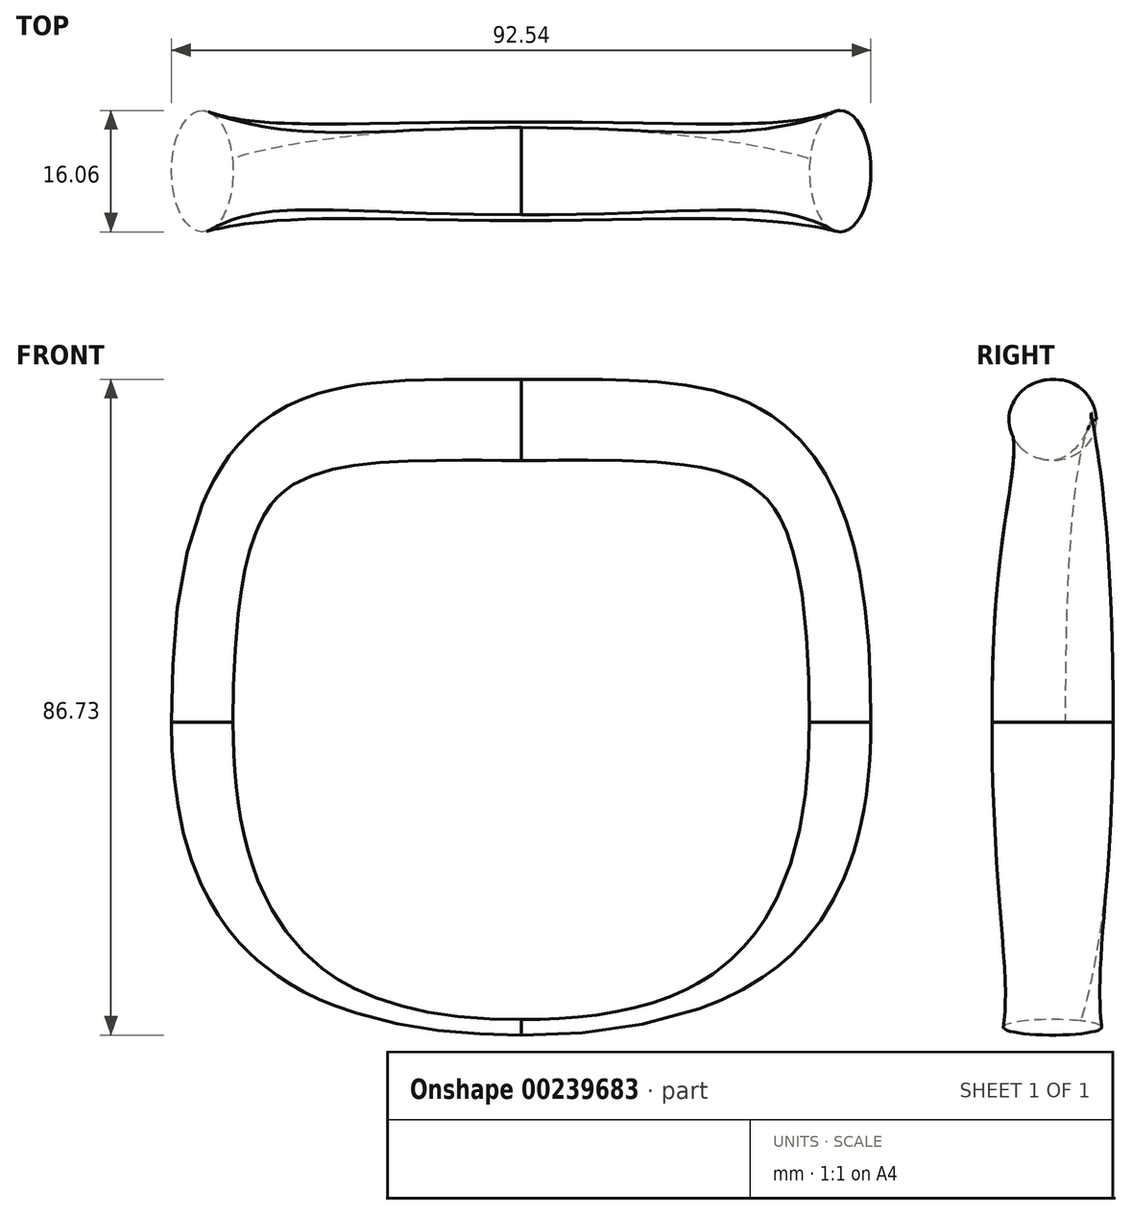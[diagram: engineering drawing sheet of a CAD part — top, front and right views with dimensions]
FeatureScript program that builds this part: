
annotation { "Feature Type Name" : "Feature", "Feature Type Description" : "" }
export const myFeature = defineFeature(function(context is Context, id is Id, definition is map)
    precondition{}
    {
        {
            var Q0;
            Q0=qCreatedBy(makeId("Right.planeOp"),FACE);
            var sketch = newSketch(context, id + "F0", { "sketchPlane" : qUnion([Q0])});
            skEllipse(sketch, "E0", {"center": v(0, 40) * mm, "majorRadius": 5.78 * mm, "minorRadius": 5.36 * mm, "majorAxis": v(1, 0)});
            skEllipse(sketch, "E1", {"center": v(0, -40.34) * mm, "majorRadius": 6.51 * mm, "minorRadius": 1.03 * mm, "majorAxis": v(1, 0)});
            skSolve(sketch);
        }
        {
            var Q0;
            Q0=qCreatedBy(makeId("Top.planeOp"),FACE);
            var sketch = newSketch(context, id + "F1", { "sketchPlane" : qUnion([Q0])});
            skEllipse(sketch, "E2", {"center": v(-42.2, 0) * mm, "majorRadius": 8.03 * mm, "minorRadius": 4.07 * mm, "majorAxis": v(0, 1)});
            skEllipse(sketch, "E3.MirrorC", {"center": v(42.2, 0) * mm, "majorRadius": 8.03 * mm, "minorRadius": 4.07 * mm, "majorAxis": v(0, 1)});
            skSolve(sketch);
        }
        {
            var Q0;
            Q0=qCreatedBy(makeId("Front.planeOp"),FACE);
            var sketch = newSketch(context, id + "F2", { "sketchPlane" : qUnion([Q0])});
            skFitSpline(sketch, "E4", {"points": [v(0, 40.05) * mm, v(42.43, 0) * mm, v(0, -40.58) * mm, v(-42.09, 0) * mm, v(0, 40.05) * mm]});
            skSolve(sketch);
        }
        {
            var Q0;
            Q0=qCreatedBy(makeId("Right.planeOp"),FACE);
            cPlane(context, id + "F3", {"entities" : qUnion([Q0]), "cplaneType" : CPlaneType.OFFSET, "offset" : 1 * mm, "oppositeDirection" : true, "width" : 150 * mm, "height" : 150 * mm});
        }
        {
            var Q0;
            Q0=makeQuery(id+"F0.imprint","IMPRINT",FACE,{"disambiguationData":[TD([[makeQuery(id+"F0.imprint","IMPRINT",EDGE,{"derivedFrom":sQuery(id+"F0.wireOp",EDGE,"E0")}),1.0]])]});
            var Q1;
            Q1=makeQuery(id+"F1.imprint","IMPRINT",FACE,{"disambiguationData":[TD([[makeQuery(id+"F1.imprint","IMPRINT",EDGE,{"derivedFrom":sQuery(id+"F1.wireOp",EDGE,"E3.MirrorC")}),1.0]])]});
            var Q2;
            Q2=sQuery(id+"F2.wireOp",EDGE,"E4");
            loft(context, id + "F4", {"startCondition" : LoftEndDerivativeType.NORMAL_TO_PROFILE, "startMagnitude" : 2, "endCondition" : LoftEndDerivativeType.NORMAL_TO_PROFILE, "endMagnitude" : 3, "sheetProfilesArray" : [{ "sheetProfileEntities" : qUnion([Q0]) }, { "sheetProfileEntities" : qUnion([Q1]) }], "guidesArray" : [{ "guideEntities" : qUnion([Q2]), "guideDerivativeType" : LoftGuideDerivativeType.DEFAULT, "guideDerivativeMagnitude" : 1 }]});
        }
        {
            var Q0;
            Q0=makeQuery(id+"F1.imprint","IMPRINT",FACE,{"disambiguationData":[TD([[makeQuery(id+"F1.imprint","IMPRINT",EDGE,{"derivedFrom":sQuery(id+"F1.wireOp",EDGE,"E3.MirrorC")}),1.0]])]});
            var Q1;
            Q1=makeQuery(id+"F0.imprint","IMPRINT",FACE,{"disambiguationData":[TD([[makeQuery(id+"F0.imprint","IMPRINT",EDGE,{"derivedFrom":sQuery(id+"F0.wireOp",EDGE,"E1")}),1.0]])]});
            loft(context, id + "F5", {"operationType" : NewBodyOperationType.ADD, "startCondition" : LoftEndDerivativeType.NORMAL_TO_PROFILE, "startMagnitude" : 2, "endCondition" : LoftEndDerivativeType.NORMAL_TO_PROFILE, "endMagnitude" : 2, "sheetProfilesArray" : [{ "sheetProfileEntities" : qUnion([Q0]) }, { "sheetProfileEntities" : qUnion([Q1]) }]});
        }
        {
            var Q0;
            Q0=makeQuery(id+"F4.opLoft","SWEPT_BODY",BODY,{"disambiguationData":[OSD([makeQuery(id+"F0.imprint","IMPRINT",FACE,{"disambiguationData":[TD([[makeQuery(id+"F0.imprint","IMPRINT",EDGE,{"derivedFrom":sQuery(id+"F0.wireOp",EDGE,"E0")}),1.0]])]}),makeQuery(id+"F1.imprint","IMPRINT",FACE,{"disambiguationData":[TD([[makeQuery(id+"F1.imprint","IMPRINT",EDGE,{"derivedFrom":sQuery(id+"F1.wireOp",EDGE,"E3.MirrorC")}),1.0]])]})])]});
            var Q1;
            Q1=qCreatedBy(makeId("Right.planeOp"),FACE);
            mirror(context, id + "F6", {"operationType" : NewBodyOperationType.ADD, "entities" : qUnion([Q0]), "mirrorPlane" : qUnion([Q1])});
        }
    });
